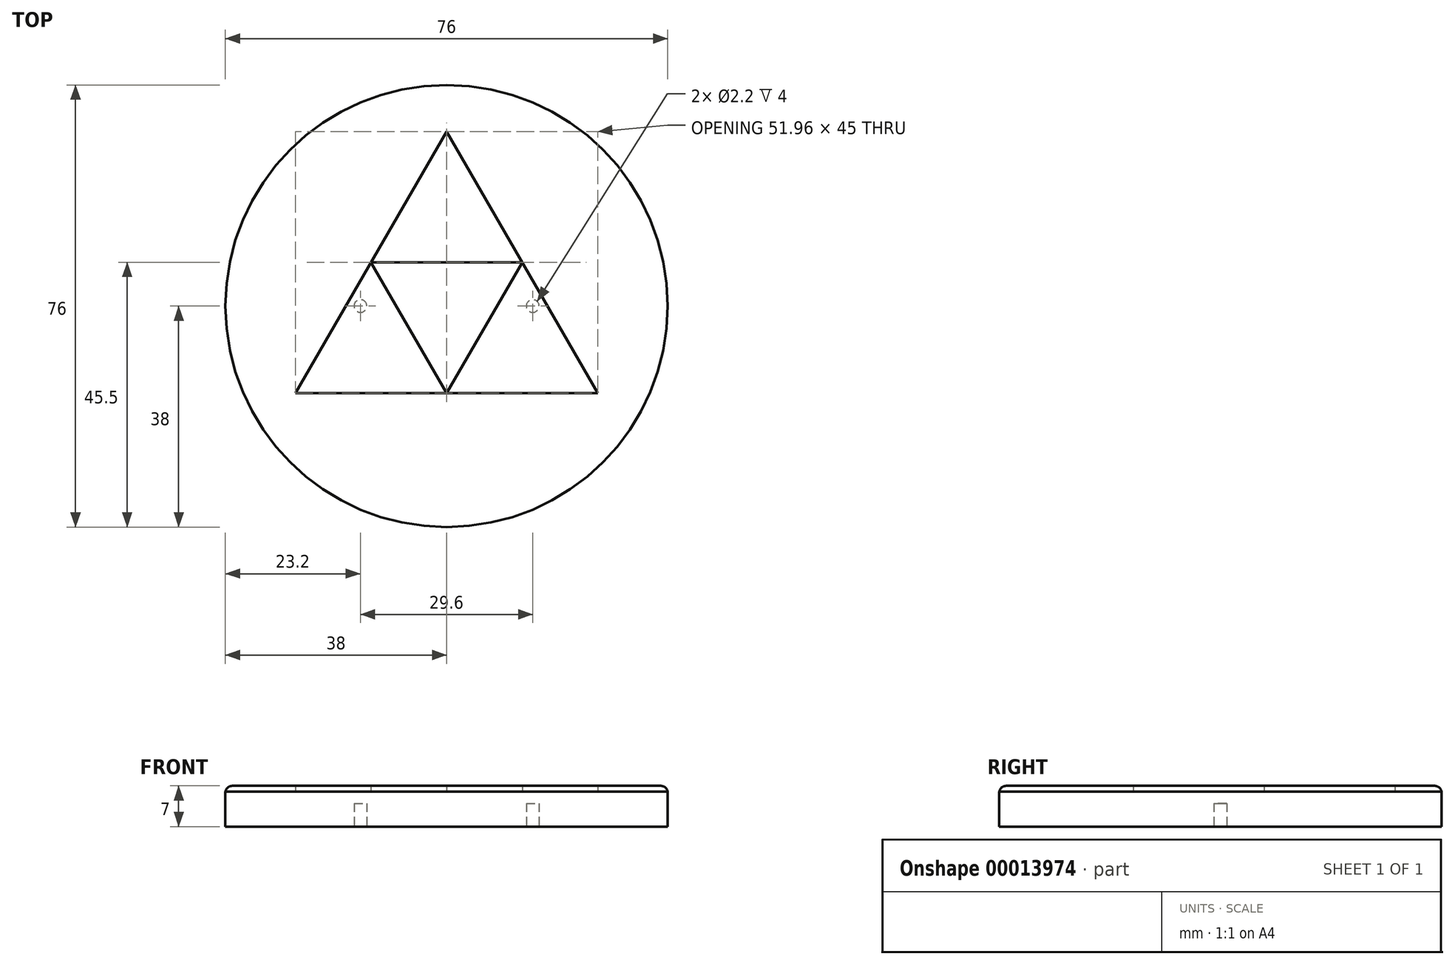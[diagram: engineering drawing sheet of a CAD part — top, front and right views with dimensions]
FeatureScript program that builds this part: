
annotation { "Feature Type Name" : "Feature", "Feature Type Description" : "" }
export const myFeature = defineFeature(function(context is Context, id is Id, definition is map)
    precondition{}
    {
        {
            var Q0;
            Q0=qCreatedBy(makeId("Top.planeOp"),FACE);
            var sketch = newSketch(context, id + "F0", { "sketchPlane" : qUnion([Q0])});
            skCircle(sketch, "E0", {"center": v(0, 0) * mm, "radius": 38 * mm});
            skCircle(sketch, "E1", {"center": v(0, 0) * mm, "radius": 30 * mm, "construction": true});
            skLineSegment(sketch, "E2", {"start": v(30, 0) * mm, "end": v(38, 0) * mm, "construction": true});
            skLineSegment(sketch, "E3", {"start": v(0, 0) * mm, "end": v(0, 30) * mm, "construction": true});
            skLineSegment(sketch, "E4", {"start": v(0, 30) * mm, "end": v(-25.98, -15) * mm});
            skLineSegment(sketch, "E5", {"start": v(-25.98, -15) * mm, "end": v(25.98, -15) * mm});
            skLineSegment(sketch, "E6", {"start": v(25.98, -15) * mm, "end": v(0, 30) * mm});
            skLineSegment(sketch, "E7", {"start": v(-13, 7.5) * mm, "end": v(0, -15) * mm});
            skLineSegment(sketch, "E8", {"start": v(0, -15) * mm, "end": v(13, 7.5) * mm});
            skLineSegment(sketch, "E9", {"start": v(13, 7.5) * mm, "end": v(-13, 7.5) * mm});
            skLineSegment(sketch, "E10.1.0", {"start": v(0, 0) * mm, "end": v(-25.98, -15) * mm, "construction": true});
            skLineSegment(sketch, "E10.2.0", {"start": v(0, 0) * mm, "end": v(25.98, -15) * mm, "construction": true});
            skSolve(sketch);
        }
        {
            var Q0;
            Q0=makeQuery(id+"F0.imprint","IMPRINT",FACE,{"disambiguationData":[TD([[makeQuery(id+"F0.imprint","IMPRINT",EDGE,{"derivedFrom":sQuery(id+"F0.wireOp",EDGE,"E0")}),1.0]])]});
            var Q1;
            Q1=makeQuery(id+"F0.imprint","IMPRINT",FACE,{"disambiguationData":[TD([[makeQuery(id+"F0.imprint","IMPRINT",EDGE,{"derivedFrom":sQuery(id+"F0.wireOp",EDGE,"E7")}),1.0]])]});
            extrude(context, id + "F1", {"entities" : qUnion([Q0, Q1]), "depth" : 1 * mm});
        }
        {
            var Q0;
            Q0=makeQuery(id+"F1.opExtrude","CAP_FACE",FACE,{"disambiguationData":[OSD([sQuery(id+"F0.wireOp",EDGE,"E0"),sQuery(id+"F0.wireOp",EDGE,"E4"),sQuery(id+"F0.wireOp",EDGE,"E5"),sQuery(id+"F0.wireOp",EDGE,"E6")])],"isStart":true});
            var sketch = newSketch(context, id + "F2", { "sketchPlane" : qUnion([Q0])});
            skCircle(sketch, "E11.0", {"center": v(0, 0) * mm, "radius": 38 * mm});
            skSolve(sketch);
        }
        {
            var Q0;
            Q0 = qSketchRegion(id + "F2", true);
            extrude(context, id + "F3", {"entities" : qUnion([Q0]), "depth" : 6 * mm});
        }
        {
            var Q0;
            Q0=makeQuery(id+"F3.opExtrude","CAP_FACE",FACE,{"disambiguationData":[OSD([sQuery(id+"F2.wireOp",EDGE,"E11.0")])],"isStart":false});
            var sketch = newSketch(context, id + "F4", { "sketchPlane" : qUnion([Q0])});
            skCircle(sketch, "E12.0", {"center": v(0, 0) * mm, "radius": 38 * mm});
            skLineSegment(sketch, "E13", {"start": v(-38, 0) * mm, "end": v(-14.8, 0) * mm, "construction": true});
            skLineSegment(sketch, "E14", {"start": v(38, 0) * mm, "end": v(14.8, 0) * mm, "construction": true});
            skCircle(sketch, "E15", {"center": v(-14.8, 0) * mm, "radius": 1.1 * mm});
            skCircle(sketch, "E16", {"center": v(14.8, 0) * mm, "radius": 1.1 * mm});
            skSolve(sketch);
        }
        {
            var Q0;
            Q0=makeQuery(id+"F4.imprint","IMPRINT",FACE,{"disambiguationData":[TD([[makeQuery(id+"F4.imprint","IMPRINT",EDGE,{"derivedFrom":sQuery(id+"F4.wireOp",EDGE,"E16")}),1.0]])]});
            var Q1;
            Q1=makeQuery(id+"F4.imprint","IMPRINT",FACE,{"disambiguationData":[TD([[makeQuery(id+"F4.imprint","IMPRINT",EDGE,{"derivedFrom":sQuery(id+"F4.wireOp",EDGE,"E15")}),1.0]])]});
            extrude(context, id + "F5", {"entities" : qUnion([Q0, Q1]), "operationType" : NewBodyOperationType.REMOVE, "oppositeDirection" : true, "depth" : 4 * mm});
        }
        {
            var Q0;
            Q0=makeQuery(id+"F1.opExtrude","CAP_EDGE",EDGE,{"disambiguationData":[OSD([sQuery(id+"F0.wireOp",EDGE,"E0")])],"isStart":false});
            fillet(context, id + "F6", {"entities" : qUnion([Q0]), "radius" : 1.2 * mm, "tangentPropagation" : true, "allowEdgeOverflow" : false});
        }
    });
